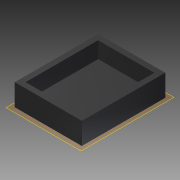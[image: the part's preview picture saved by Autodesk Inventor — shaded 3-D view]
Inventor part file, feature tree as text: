
AUTODESK INVENTOR PART (.ipt)
format: ipt  version: 2014 (Build 180170000, 170)  size: 100,864 bytes
history: native  units: mm
features: extrude x2, sketch x2, plane x1, reference x1
ambient origin geometry x8: Origin, YZ Plane, XZ Plane, XY Plane, X Axis, Y Axis, Z Axis, Center Point
bodies: Volumenkörper1 (feature_tree)
feature tree (6):
  plane  "Arbeitsebene1"
  extrude  "Extrusion1"  Depth=5.0mm TaperAngle=0.0deg
  extrude  "Extrusion2"  Depth=15.0mm TaperAngle=0.0deg
  sketch  "Skizze1"  dims[d0=0.5mm d1=5.0mm d2=0.0mm]
  reference  "Referenz1"
  sketch  "Skizze2"  dims[d3=5.0mm d4=15.0mm d5=0.0mm]
